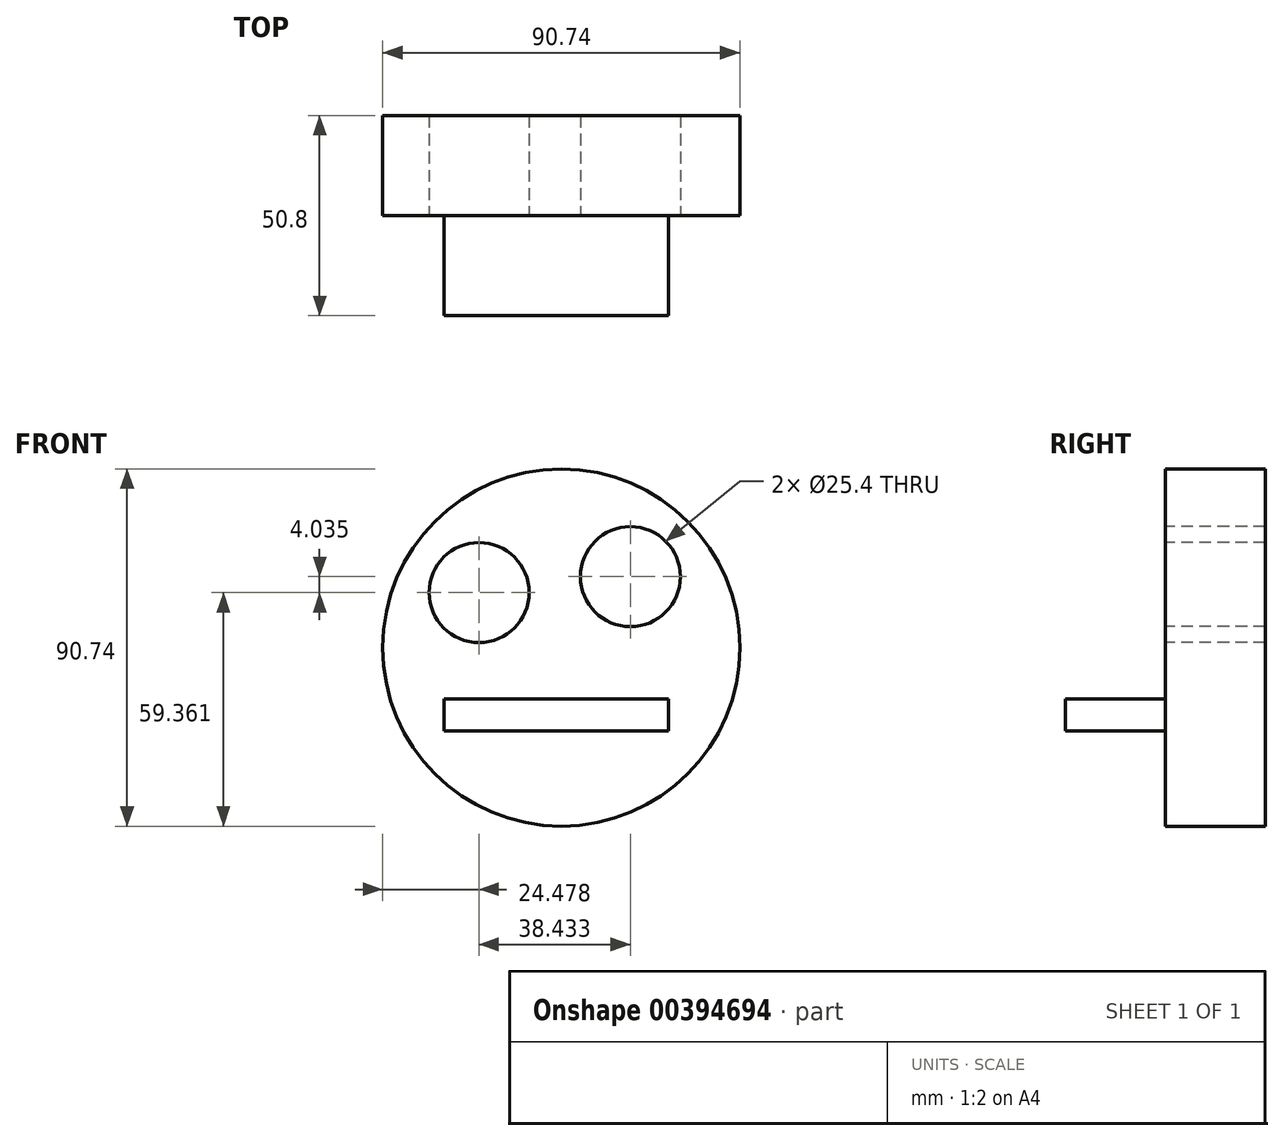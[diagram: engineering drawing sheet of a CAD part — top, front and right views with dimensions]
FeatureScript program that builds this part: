
annotation { "Feature Type Name" : "Feature", "Feature Type Description" : "" }
export const myFeature = defineFeature(function(context is Context, id is Id, definition is map)
    precondition{}
    {
        {
            var Q0;
            Q0=qCreatedBy(makeId("Front.planeOp"),FACE);
            var sketch = newSketch(context, id + "F0", { "sketchPlane" : qUnion([Q0])});
            skCircle(sketch, "E0", {"center": v(-15.43, 7.75) * mm, "radius": 45.37 * mm});
            skSolve(sketch);
        }
        {
            var Q0;
            Q0=makeQuery(id+"F0.imprint","IMPRINT",FACE,{"disambiguationData":[TD([[makeQuery(id+"F0.imprint","IMPRINT",EDGE,{"derivedFrom":sQuery(id+"F0.wireOp",EDGE,"E0")}),1.0]])]});
            extrude(context, id + "F1", {"entities" : qUnion([Q0]), "depth" : 25.4 * mm});
        }
        {
            var Q0;
            Q0=makeQuery(id+"F1.opExtrude","CAP_FACE",FACE,{"disambiguationData":[OSD([sQuery(id+"F0.wireOp",EDGE,"E0")])],"isStart":false});
            var sketch = newSketch(context, id + "F2", { "sketchPlane" : qUnion([Q0])});
            skPoint(sketch, "E1", {"position": v(-36.32, 21.74) * mm});
            skSolve(sketch);
        }
        {
            var Q0;
            Q0=sQuery(id+"F2.wireOp",VERTEX,"E1");
            var Q1;
            Q1=makeQuery(id+"F1.opExtrude","SWEPT_BODY",BODY,{"disambiguationData":[OSD([sQuery(id+"F0.wireOp",EDGE,"E0")])]});
            hole(context, id + "F3", {"style" : HoleStyle.SIMPLE, "endStyle" : HoleEndStyle.THROUGH, "holeDiameter" : 25.4 * mm, "isTappedThrough" : true, "tappedDepth" : 12.7 * mm, "tapClearance" : 3, "locations" : qUnion([Q0]), "scope" : qUnion([Q1])});
        }
        {
            var Q0;
            Q0=makeQuery(id+"F1.opExtrude","CAP_FACE",FACE,{"disambiguationData":[OSD([sQuery(id+"F0.wireOp",EDGE,"E0")])],"isStart":false});
            var sketch = newSketch(context, id + "F4", { "sketchPlane" : qUnion([Q0])});
            skPoint(sketch, "E2", {"position": v(2.11, 25.78) * mm});
            skSolve(sketch);
        }
        {
            var Q0;
            Q0=sQuery(id+"F4.wireOp",VERTEX,"E2");
            var Q1;
            Q1=makeQuery(id+"F1.opExtrude","SWEPT_BODY",BODY,{"disambiguationData":[OSD([sQuery(id+"F0.wireOp",EDGE,"E0")])]});
            hole(context, id + "F5", {"style" : HoleStyle.SIMPLE, "endStyle" : HoleEndStyle.THROUGH, "holeDiameter" : 25.4 * mm, "isTappedThrough" : true, "tappedDepth" : 12.7 * mm, "tapClearance" : 3, "locations" : qUnion([Q0]), "scope" : qUnion([Q1])});
        }
        {
            var Q0;
            Q0=makeQuery(id+"F1.opExtrude","CAP_FACE",FACE,{"disambiguationData":[OSD([sQuery(id+"F0.wireOp",EDGE,"E0")])],"isStart":false});
            var sketch = newSketch(context, id + "F6", { "sketchPlane" : qUnion([Q0])});
            skLineSegment(sketch, "E3.bottom", {"start": v(-45.21, -13.47) * mm, "end": v(11.75, -13.47) * mm});
            skLineSegment(sketch, "E3.top", {"start": v(-45.21, -5.34) * mm, "end": v(11.75, -5.34) * mm});
            skLineSegment(sketch, "E3.left", {"start": v(-45.21, -13.47) * mm, "end": v(-45.21, -5.34) * mm});
            skLineSegment(sketch, "E3.right", {"start": v(11.75, -13.47) * mm, "end": v(11.75, -5.34) * mm});
            skSolve(sketch);
        }
        {
            var Q0;
            Q0=makeQuery(id+"F6.imprint","IMPRINT",FACE,{"disambiguationData":[TD([[makeQuery(id+"F6.imprint","IMPRINT",EDGE,{"derivedFrom":sQuery(id+"F6.wireOp",EDGE,"E3.bottom")}),1.0]])]});
            extrude(context, id + "F7", {"entities" : qUnion([Q0]), "operationType" : NewBodyOperationType.ADD, "depth" : 25.4 * mm});
        }
    });
